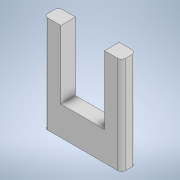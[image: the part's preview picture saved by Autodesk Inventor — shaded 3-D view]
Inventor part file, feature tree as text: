
AUTODESK INVENTOR PART (.ipt)
format: ipt  version: 2021 (Build 250183000, 183)  size: 122,368 bytes
history: native  units: in
note: dims shown in document units (in); Inventor stores cm internally (conversion verified against a paired STEP export)
features: extrude x2, sketch x2, fillet x1, projected_geometry x1
ambient origin geometry x8: Origin, YZ Plane, XZ Plane, XY Plane, X Axis, Y Axis, Z Axis, Center Point
bodies: Solid1 (feature_tree)
feature tree (6):
  extrude  "Extrusion1"  Depth=0.3937in
  extrude  "Extrusion2"  Depth=0.1772in
  fillet  "Fillet1"  Radius=0.2756in
  sketch  "Sketch1"  dims[d0=0.315in d1=0.3937in]
  sketch  "Sketch2"  dims[d2=0.0591in d3=0.0in d4=0.1772in d5=0.2756in d6=0.0in d7=0.0in d8=0.0157in]
  projected_geometry  "Projected Loop1"
